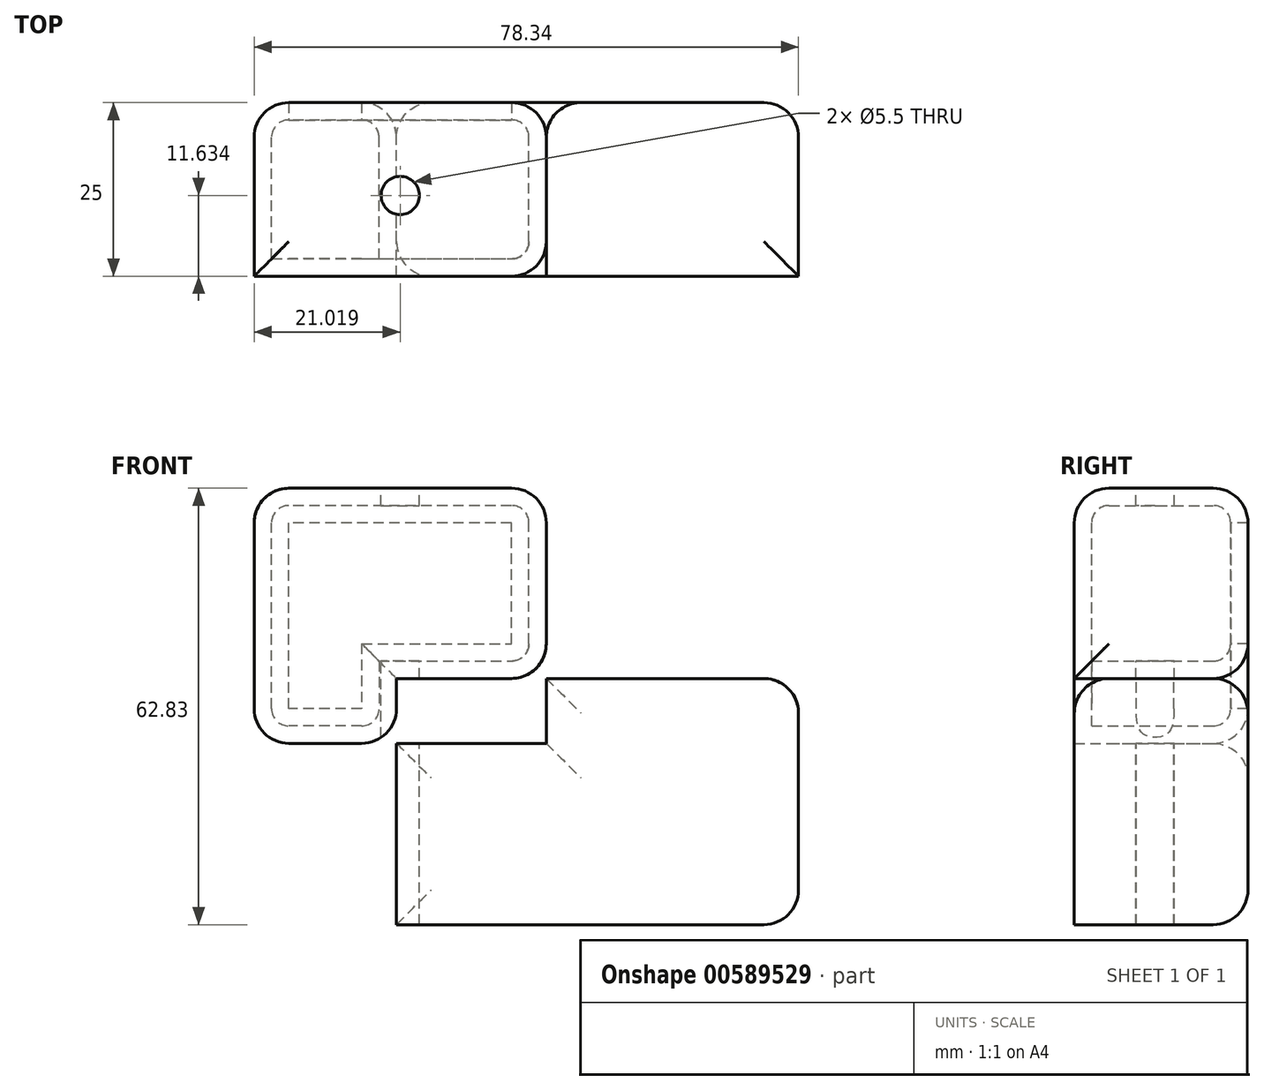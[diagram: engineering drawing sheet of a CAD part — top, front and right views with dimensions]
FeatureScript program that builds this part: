
annotation { "Feature Type Name" : "Feature", "Feature Type Description" : "" }
export const myFeature = defineFeature(function(context is Context, id is Id, definition is map)
    precondition{}
    {
        {
            var Q0;
            Q0=qCreatedBy(makeId("Front.planeOp"),FACE);
            var sketch = newSketch(context, id + "F0", { "sketchPlane" : qUnion([Q0])});
            skLineSegment(sketch, "E0.bottom", {"start": v(-30.44, 15.37) * mm, "end": v(27.43, 15.37) * mm});
            skLineSegment(sketch, "E0.top", {"start": v(-30.44, -20.06) * mm, "end": v(27.43, -20.06) * mm});
            skLineSegment(sketch, "E0.left", {"start": v(-30.44, 15.37) * mm, "end": v(-30.44, -20.06) * mm});
            skLineSegment(sketch, "E0.right", {"start": v(27.43, 15.37) * mm, "end": v(27.43, -20.06) * mm});
            skLineSegment(sketch, "E1.bottom", {"start": v(-8.87, 6.04) * mm, "end": v(-50.91, 6.04) * mm});
            skLineSegment(sketch, "E1.top", {"start": v(-8.87, 42.77) * mm, "end": v(-50.91, 42.77) * mm});
            skLineSegment(sketch, "E1.left", {"start": v(-8.87, 6.04) * mm, "end": v(-8.87, 42.77) * mm});
            skLineSegment(sketch, "E1.right", {"start": v(-50.91, 6.04) * mm, "end": v(-50.91, 42.77) * mm});
            skSolve(sketch);
        }
        {
            var Q0;
            {var subQ4=sQuery(id+"F0.wireOp",EDGE,"E1.top");Q0=makeQuery(id+"F0.imprint","IMPRINT",FACE,{"disambiguationData":[TD([[makeQuery(id+"F0.imprint","IMPRINT",EDGE,{"derivedFrom":subQ4}),1.0]])]});}
            var Q1;
            {var subQ2=sQuery(id+"F0.wireOp",EDGE,"E0.top");Q1=makeQuery(id+"F0.imprint","IMPRINT",FACE,{"disambiguationData":[TD([[makeQuery(id+"F0.imprint","IMPRINT",EDGE,{"derivedFrom":subQ2}),1.0]])]});}
            extrude(context, id + "F1", {"entities" : qUnion([Q0, Q1]), "depth" : 25 * mm, "offsetDistance" : 25 * mm});
        }
        {
            var Q0;
            Q0=makeQuery(id+"F1.opExtrude","SWEPT_EDGE",EDGE,{"disambiguationData":[OSD([sQuery(id+"F0.wireOp",EDGE,"E1.top"),sQuery(id+"F0.wireOp",EDGE,"E1.left")])]});
            var Q1;
            Q1=makeQuery(id+"F1.opExtrude","SWEPT_EDGE",EDGE,{"disambiguationData":[OSD([sQuery(id+"F0.wireOp",EDGE,"E1.top"),sQuery(id+"F0.wireOp",EDGE,"E1.right")])]});
            var Q2;
            Q2=makeQuery(id+"F1.opExtrude","SWEPT_EDGE",EDGE,{"disambiguationData":[OSD([sQuery(id+"F0.wireOp",EDGE,"E0.bottom"),sQuery(id+"F0.wireOp",EDGE,"E0.right")])]});
            var Q3;
            Q3=makeQuery(id+"F1.opExtrude","SWEPT_EDGE",EDGE,{"disambiguationData":[OSD([sQuery(id+"F0.wireOp",EDGE,"E0.top"),sQuery(id+"F0.wireOp",EDGE,"E0.right")])]});
            var Q4;
            {var subQ0=sQuery(id+"F0.wireOp",EDGE,"E0.bottom");Q4=makeQuery(id+"F1.opExtrude","CAP_EDGE",EDGE,{"disambiguationData":[OSD([subQ0]),TDD([makeQuery(id+"F0.imprint","IMPRINT",EDGE,{"disambiguationData":[TD([[makeQuery(id+"F0.imprint","INTERSECT",VERTEX,{"derivedFrom":[subQ0,sQuery(id+"F0.wireOp",EDGE,"E0.right")]}),1.0]])],"derivedFrom":subQ0})])],"isStart":false});}
            var Q5;
            Q5=makeQuery(id+"F1.opExtrude","SWEPT_EDGE",EDGE,{"disambiguationData":[OSD([sQuery(id+"F0.wireOp",EDGE,"E1.bottom"),sQuery(id+"F0.wireOp",EDGE,"E1.right")])]});
            var Q6;
            Q6=makeQuery(id+"F1.opExtrude","SWEPT_EDGE",EDGE,{"disambiguationData":[OSD([sQuery(id+"F0.wireOp",EDGE,"E0.left"),sQuery(id+"F0.wireOp",EDGE,"E1.bottom")]),OD(1.0)]});
            var Q7;
            Q7=makeQuery(id+"F1.opExtrude","SWEPT_EDGE",EDGE,{"disambiguationData":[OSD([sQuery(id+"F0.wireOp",EDGE,"E0.bottom"),sQuery(id+"F0.wireOp",EDGE,"E1.left")]),OD(1.0)]});
            var Q8;
            {var subQ0=sQuery(id+"F0.wireOp",EDGE,"E1.left");Q8=makeQuery(id+"F1.opExtrude","CAP_EDGE",EDGE,{"disambiguationData":[OSD([subQ0]),TDD([makeQuery(id+"F0.imprint","IMPRINT",EDGE,{"disambiguationData":[TD([[makeQuery(id+"F0.imprint","INTERSECT",VERTEX,{"derivedFrom":[sQuery(id+"F0.wireOp",EDGE,"E1.top"),subQ0]}),1.0]])],"derivedFrom":subQ0})])],"isStart":false});}
            var Q9;
            Q9=makeQuery(id+"F1.opExtrude","CAP_EDGE",EDGE,{"disambiguationData":[OSD([sQuery(id+"F0.wireOp",EDGE,"E1.top")])],"isStart":false});
            var Q10;
            Q10=makeQuery(id+"F1.opExtrude","CAP_FACE",FACE,{"disambiguationData":[OSD([sQuery(id+"F0.wireOp",EDGE,"E0.bottom"),sQuery(id+"F0.wireOp",EDGE,"E0.top"),sQuery(id+"F0.wireOp",EDGE,"E0.left"),sQuery(id+"F0.wireOp",EDGE,"E0.right"),sQuery(id+"F0.wireOp",EDGE,"E1.bottom"),sQuery(id+"F0.wireOp",EDGE,"E1.left")])],"isStart":true});
            var Q11;
            Q11=makeQuery(id+"F1.opExtrude","CAP_FACE",FACE,{"disambiguationData":[OSD([sQuery(id+"F0.wireOp",EDGE,"E0.bottom"),sQuery(id+"F0.wireOp",EDGE,"E0.left"),sQuery(id+"F0.wireOp",EDGE,"E1.bottom"),sQuery(id+"F0.wireOp",EDGE,"E1.top"),sQuery(id+"F0.wireOp",EDGE,"E1.left"),sQuery(id+"F0.wireOp",EDGE,"E1.right")])],"isStart":true});
            var Q12;
            {var subQ0=sQuery(id+"F0.wireOp",EDGE,"E0.left");Q12=makeQuery(id+"F1.opExtrude","CAP_EDGE",EDGE,{"disambiguationData":[OSD([subQ0]),TDD([makeQuery(id+"F0.imprint","IMPRINT",EDGE,{"disambiguationData":[TD([[makeQuery(id+"F0.imprint","INTERSECT",VERTEX,{"derivedFrom":[sQuery(id+"F0.wireOp",EDGE,"E0.top"),subQ0]}),1.0]])],"derivedFrom":subQ0})])],"isStart":false});}
            fillet(context, id + "F2", {"entities" : qUnion([Q0, Q1, Q2, Q3, Q4, Q5, Q6, Q7, Q8, Q9, Q10, Q11, Q12]), "radius" : 5 * mm, "tangentPropagation" : true, "allowEdgeOverflow" : false});
        }
        {
            var Q0;
            Q0=makeQuery(id+"F1.opExtrude","CAP_FACE",FACE,{"disambiguationData":[OSD([sQuery(id+"F0.wireOp",EDGE,"E0.bottom"),sQuery(id+"F0.wireOp",EDGE,"E0.left"),sQuery(id+"F0.wireOp",EDGE,"E1.bottom"),sQuery(id+"F0.wireOp",EDGE,"E1.top"),sQuery(id+"F0.wireOp",EDGE,"E1.left"),sQuery(id+"F0.wireOp",EDGE,"E1.right")])],"isStart":true});
            shell(context, id + "F3", {"entities" : qUnion([Q0]), "thickness" : 2.5 * mm});
        }
        {
            var Q0;
            Q0=makeQuery(id+"F1.opExtrude","SWEPT_FACE",FACE,{"disambiguationData":[OSD([sQuery(id+"F0.wireOp",EDGE,"E1.top")])]});
            var sketch = newSketch(context, id + "F4", { "sketchPlane" : qUnion([Q0])});
            skPoint(sketch, "E2", {"position": v(-29.9, -13.37) * mm});
            skPoint(sketch, "E2.positionSnap0", {"position": v(-29.9, -5) * mm});
            skSolve(sketch);
        }
        {
            var Q0;
            Q0=sQuery(id+"F4.wireOp",VERTEX,"E2");
            var Q1;
            Q1=makeQuery(id+"F1.opExtrude","SWEPT_BODY",BODY,{"disambiguationData":[OSD([sQuery(id+"F0.wireOp",EDGE,"E0.bottom"),sQuery(id+"F0.wireOp",EDGE,"E0.left"),sQuery(id+"F0.wireOp",EDGE,"E1.bottom"),sQuery(id+"F0.wireOp",EDGE,"E1.top"),sQuery(id+"F0.wireOp",EDGE,"E1.left"),sQuery(id+"F0.wireOp",EDGE,"E1.right")])]});
            var Q2;
            Q2=makeQuery(id+"F1.opExtrude","SWEPT_BODY",BODY,{"disambiguationData":[OSD([sQuery(id+"F0.wireOp",EDGE,"E0.bottom"),sQuery(id+"F0.wireOp",EDGE,"E0.top"),sQuery(id+"F0.wireOp",EDGE,"E0.left"),sQuery(id+"F0.wireOp",EDGE,"E0.right"),sQuery(id+"F0.wireOp",EDGE,"E1.bottom"),sQuery(id+"F0.wireOp",EDGE,"E1.left")])]});
            hole(context, id + "F5", {"style" : HoleStyle.SIMPLE, "endStyle" : HoleEndStyle.THROUGH, "standardTappedOrClearance" : lookupTablePath({ "standard" : "ISO", "fit" : "Normal", "size" : "M5", "type" : "Clearance" }), "standardBlindInLast" : lookupTablePath({ "fit" : "Standard", "standard" : "ISO", "size" : "M5", "type" : "Clearance" }), "holeDiameter" : 5.5 * mm, "majorDiameter" : 5 * mm, "isTappedThrough" : true, "tappedDepth" : 12 * mm, "tapClearance" : 3, "locations" : qUnion([Q0]), "scope" : qUnion([Q1, Q2])});
        }
    });
